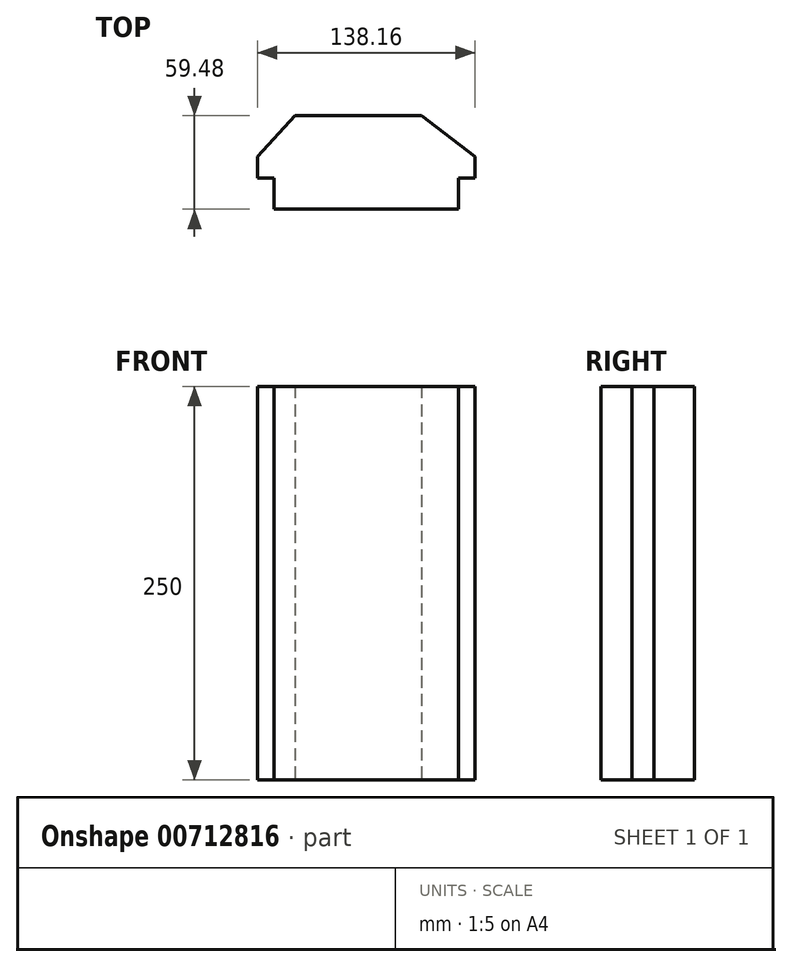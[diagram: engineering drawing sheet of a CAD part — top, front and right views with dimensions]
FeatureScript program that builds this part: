
annotation { "Feature Type Name" : "Feature", "Feature Type Description" : "" }
export const myFeature = defineFeature(function(context is Context, id is Id, definition is map)
    precondition{}
    {
        {
            var Q0;
            Q0=qCreatedBy(makeId("Top.planeOp"),FACE);
            var sketch = newSketch(context, id + "F0", { "sketchPlane" : qUnion([Q0])});
            skLineSegment(sketch, "E0", {"start": v(-58.6, -52.43) * mm, "end": v(58.6, -52.43) * mm});
            skLineSegment(sketch, "E1", {"start": v(58.6, -52.43) * mm, "end": v(58.6, -32.78) * mm});
            skLineSegment(sketch, "E2", {"start": v(58.6, -32.78) * mm, "end": v(69.08, -32.78) * mm});
            skLineSegment(sketch, "E3", {"start": v(69.08, -32.78) * mm, "end": v(69.08, -18.88) * mm});
            skLineSegment(sketch, "E4.MirrorCS", {"start": v(-69.08, -32.78) * mm, "end": v(-69.08, -18.88) * mm});
            skLineSegment(sketch, "E5.MirrorCS", {"start": v(-58.6, -32.78) * mm, "end": v(-69.08, -32.78) * mm});
            skLineSegment(sketch, "E6.MirrorCS", {"start": v(-58.6, -52.43) * mm, "end": v(-58.6, -32.78) * mm});
            skLineSegment(sketch, "E7", {"start": v(-45.4, 7.05) * mm, "end": v(35.03, 7.05) * mm});
            skLineSegment(sketch, "E8", {"start": v(-45.4, 7.05) * mm, "end": v(-69.08, -18.88) * mm});
            skLineSegment(sketch, "E9", {"start": v(35.03, 7.05) * mm, "end": v(69.08, -18.88) * mm});
            skSolve(sketch);
        }
        {
            var Q0;
            Q0 = qSketchRegion(id + "F0", true);
            extrude(context, id + "F1", {"entities" : qUnion([Q0]), "depth" : 250 * mm, "offsetDistance" : 25.4 * mm});
        }
    });
